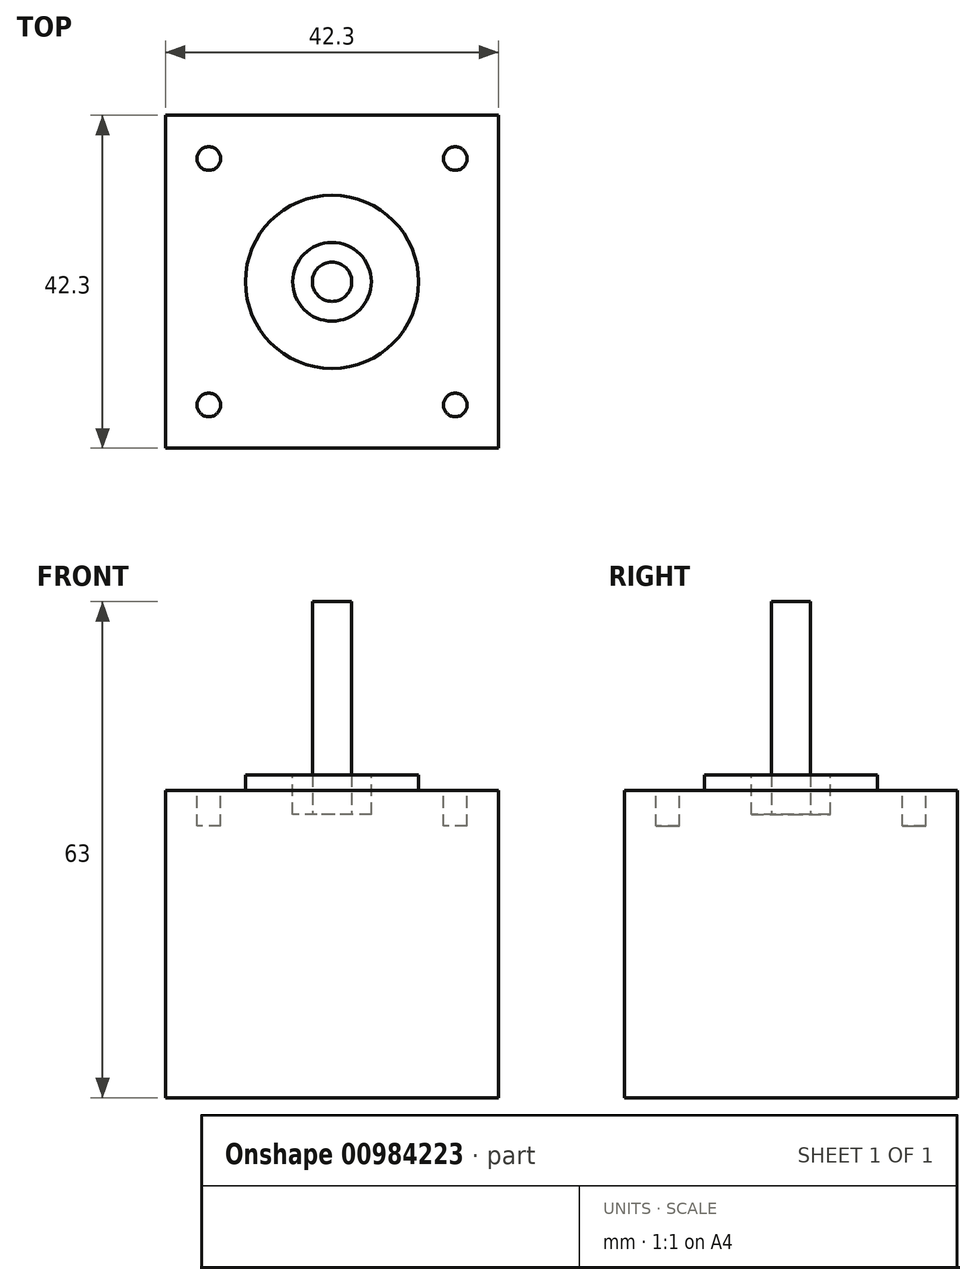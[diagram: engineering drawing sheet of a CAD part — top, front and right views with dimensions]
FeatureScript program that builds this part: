
annotation { "Feature Type Name" : "Feature", "Feature Type Description" : "" }
export const myFeature = defineFeature(function(context is Context, id is Id, definition is map)
    precondition{}
    {
        {
            var Q0;
            Q0=qCreatedBy(makeId("Top.planeOp"),FACE);
            var sketch = newSketch(context, id + "F0", { "sketchPlane" : qUnion([Q0])});
            skLineSegment(sketch, "E0.bottom", {"start": v(21.15, 21.15) * mm, "end": v(-21.15, 21.15) * mm});
            skLineSegment(sketch, "E0.top", {"start": v(21.15, -21.15) * mm, "end": v(-21.15, -21.15) * mm});
            skLineSegment(sketch, "E0.left", {"start": v(21.15, 21.15) * mm, "end": v(21.15, -21.15) * mm});
            skLineSegment(sketch, "E0.right", {"start": v(-21.15, 21.15) * mm, "end": v(-21.15, -21.15) * mm});
            skPoint(sketch, "E0.middle", {"position": v(0, 0) * mm});
            skSolve(sketch);
        }
        {
            var Q0;
            Q0=makeQuery(id+"F0.imprint","IMPRINT",FACE,{"disambiguationData":[TD([[makeQuery(id+"F0.imprint","IMPRINT",EDGE,{"derivedFrom":sQuery(id+"F0.wireOp",EDGE,"E0.bottom")}),1.0]])]});
            extrude(context, id + "F1", {"entities" : qUnion([Q0]), "depth" : 39 * mm, "offsetDistance" : 25 * mm});
        }
        {
            var Q0;
            Q0=makeQuery(id+"F1.opExtrude","CAP_FACE",FACE,{"disambiguationData":[OSD([sQuery(id+"F0.wireOp",EDGE,"E0.bottom"),sQuery(id+"F0.wireOp",EDGE,"E0.top"),sQuery(id+"F0.wireOp",EDGE,"E0.left"),sQuery(id+"F0.wireOp",EDGE,"E0.right")])],"isStart":false});
            var sketch = newSketch(context, id + "F2", { "sketchPlane" : qUnion([Q0])});
            skCircle(sketch, "E1", {"center": v(0, 0) * mm, "radius": 11 * mm});
            skSolve(sketch);
        }
        {
            var Q0;
            Q0=makeQuery(id+"F2.imprint","IMPRINT",FACE,{"disambiguationData":[TD([[makeQuery(id+"F2.imprint","IMPRINT",EDGE,{"derivedFrom":sQuery(id+"F2.wireOp",EDGE,"E1")}),1.0]])]});
            extrude(context, id + "F3", {"entities" : qUnion([Q0]), "operationType" : NewBodyOperationType.ADD, "depth" : 2 * mm, "offsetDistance" : 25 * mm});
        }
        {
            var Q0;
            Q0=makeQuery(id+"F1.opExtrude","CAP_FACE",FACE,{"disambiguationData":[OSD([sQuery(id+"F0.wireOp",EDGE,"E0.bottom"),sQuery(id+"F0.wireOp",EDGE,"E0.top"),sQuery(id+"F0.wireOp",EDGE,"E0.left"),sQuery(id+"F0.wireOp",EDGE,"E0.right")])],"isStart":false});
            var sketch = newSketch(context, id + "F4", { "sketchPlane" : qUnion([Q0])});
            skCircle(sketch, "E2", {"center": v(15.65, 15.65) * mm, "radius": 1.5 * mm});
            skSolve(sketch);
        }
        {
            var Q0;
            Q0=makeQuery(id+"F4.imprint","IMPRINT",FACE,{"disambiguationData":[TD([[makeQuery(id+"F4.imprint","IMPRINT",EDGE,{"derivedFrom":sQuery(id+"F4.wireOp",EDGE,"E2")}),1.0]])]});
            extrude(context, id + "F5", {"entities" : qUnion([Q0]), "operationType" : NewBodyOperationType.REMOVE, "oppositeDirection" : true, "depth" : 4.5 * mm, "offsetDistance" : 25 * mm});
        }
        {
            var Q0;
            Q0=makeQuery(id+"F1.opExtrude","CAP_FACE",FACE,{"disambiguationData":[OSD([sQuery(id+"F0.wireOp",EDGE,"E0.bottom"),sQuery(id+"F0.wireOp",EDGE,"E0.top"),sQuery(id+"F0.wireOp",EDGE,"E0.left"),sQuery(id+"F0.wireOp",EDGE,"E0.right")])],"isStart":false});
            var sketch = newSketch(context, id + "F6", { "sketchPlane" : qUnion([Q0])});
            skCircle(sketch, "E3", {"center": v(15.65, -15.65) * mm, "radius": 1.5 * mm});
            skSolve(sketch);
        }
        {
            var Q0;
            Q0=makeQuery(id+"F6.imprint","IMPRINT",FACE,{"disambiguationData":[TD([[makeQuery(id+"F6.imprint","IMPRINT",EDGE,{"derivedFrom":sQuery(id+"F6.wireOp",EDGE,"E3")}),1.0]])]});
            extrude(context, id + "F7", {"entities" : qUnion([Q0]), "operationType" : NewBodyOperationType.REMOVE, "oppositeDirection" : true, "depth" : 4.5 * mm, "offsetDistance" : 25 * mm});
        }
        {
            var Q0;
            Q0=makeQuery(id+"F1.opExtrude","CAP_FACE",FACE,{"disambiguationData":[OSD([sQuery(id+"F0.wireOp",EDGE,"E0.bottom"),sQuery(id+"F0.wireOp",EDGE,"E0.top"),sQuery(id+"F0.wireOp",EDGE,"E0.left"),sQuery(id+"F0.wireOp",EDGE,"E0.right")])],"isStart":false});
            var sketch = newSketch(context, id + "F8", { "sketchPlane" : qUnion([Q0])});
            skCircle(sketch, "E4", {"center": v(-15.65, -15.65) * mm, "radius": 1.5 * mm});
            skSolve(sketch);
        }
        {
            var Q0;
            Q0=makeQuery(id+"F8.imprint","IMPRINT",FACE,{"disambiguationData":[TD([[makeQuery(id+"F8.imprint","IMPRINT",EDGE,{"derivedFrom":sQuery(id+"F8.wireOp",EDGE,"E4")}),1.0]])]});
            extrude(context, id + "F9", {"entities" : qUnion([Q0]), "operationType" : NewBodyOperationType.REMOVE, "oppositeDirection" : true, "depth" : 4.5 * mm, "offsetDistance" : 25 * mm});
        }
        {
            var Q0;
            Q0=makeQuery(id+"F1.opExtrude","CAP_FACE",FACE,{"disambiguationData":[OSD([sQuery(id+"F0.wireOp",EDGE,"E0.bottom"),sQuery(id+"F0.wireOp",EDGE,"E0.top"),sQuery(id+"F0.wireOp",EDGE,"E0.left"),sQuery(id+"F0.wireOp",EDGE,"E0.right")])],"isStart":false});
            var sketch = newSketch(context, id + "F10", { "sketchPlane" : qUnion([Q0])});
            skCircle(sketch, "E5", {"center": v(-15.65, 15.65) * mm, "radius": 1.5 * mm});
            skSolve(sketch);
        }
        {
            var Q0;
            Q0=makeQuery(id+"F10.imprint","IMPRINT",FACE,{"disambiguationData":[TD([[makeQuery(id+"F10.imprint","IMPRINT",EDGE,{"derivedFrom":sQuery(id+"F10.wireOp",EDGE,"E5")}),1.0]])]});
            extrude(context, id + "F11", {"entities" : qUnion([Q0]), "operationType" : NewBodyOperationType.REMOVE, "oppositeDirection" : true, "depth" : 4.5 * mm, "offsetDistance" : 25 * mm});
        }
        {
            var Q0;
            Q0=makeQuery(id+"F3.opExtrude","CAP_FACE",FACE,{"disambiguationData":[OSD([sQuery(id+"F2.wireOp",EDGE,"E1")])],"isStart":false});
            var sketch = newSketch(context, id + "F12", { "sketchPlane" : qUnion([Q0])});
            skCircle(sketch, "E6", {"center": v(0, 0) * mm, "radius": 5 * mm});
            skSolve(sketch);
        }
        {
            var Q0;
            Q0=makeQuery(id+"F12.imprint","IMPRINT",FACE,{"disambiguationData":[TD([[makeQuery(id+"F12.imprint","IMPRINT",EDGE,{"derivedFrom":sQuery(id+"F12.wireOp",EDGE,"E6")}),1.0]])]});
            extrude(context, id + "F13", {"entities" : qUnion([Q0]), "operationType" : NewBodyOperationType.REMOVE, "oppositeDirection" : true, "depth" : 5 * mm, "offsetDistance" : 25 * mm});
        }
        {
            var Q0;
            Q0=makeQuery(id+"F13.boolean.opBoolean","COPY",FACE,{"derivedFrom":makeQuery(id+"F13.opExtrude","CAP_FACE",FACE,{"disambiguationData":[OSD([sQuery(id+"F12.wireOp",EDGE,"E6")])],"isStart":false})});
            var sketch = newSketch(context, id + "F14", { "sketchPlane" : qUnion([Q0])});
            skCircle(sketch, "E7", {"center": v(0, 0) * mm, "radius": 2.5 * mm});
            skSolve(sketch);
        }
        {
            var Q0;
            Q0=makeQuery(id+"F14.imprint","IMPRINT",FACE,{"disambiguationData":[TD([[makeQuery(id+"F14.imprint","IMPRINT",EDGE,{"derivedFrom":sQuery(id+"F14.wireOp",EDGE,"E7")}),1.0]])]});
            extrude(context, id + "F15", {"entities" : qUnion([Q0]), "operationType" : NewBodyOperationType.ADD, "depth" : 27 * mm, "offsetDistance" : 25 * mm});
        }
    });
